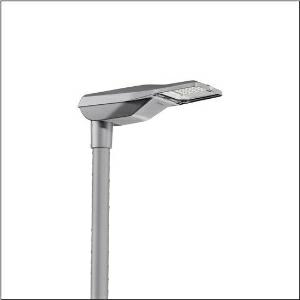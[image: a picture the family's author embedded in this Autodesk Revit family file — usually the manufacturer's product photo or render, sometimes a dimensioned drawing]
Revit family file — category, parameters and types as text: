
# Revit family: streetlight_sl_21_iq_micro___p0_5a_5xe1v31g08cb_6456
name_source: partatom
category: Lighting Fixtures
units: mm (PartAtom-declared; Revit-internal decimal feet)

## family parameters
Cut with Voids When Loaded = No
Host = Face
Light Source = No
Part Type = Normal
Room Calculation Point = No
Round Connector Dimension = Use Diameter
Shared = No

## types (1)
- --- (1 x LED, 2780 lm, 19.4 W, 3000K)
    Apparent Load = 19 VA
    CIE Flux Codes = 37 73 96 100 100
    Color Rendering = 70
    Color Temperature = 3000K
    Default Elevation = 1800 mm
    Description = Streetlight SL 21 iQ micro, mast luminaire, primary light control with lens, of PMMA, primary optical cover: cover, of toughened safety glass, transparent, light distribution: P0.5a, light emission: direct distribution, primary light characteristic: asymmetric, installation type: post-top, side-entry, LED, High Power LED, rated luminous flux: 2.780lm, luminous efficacy: 143lm/W, light colour: 730, colour temperature: 3000K, control gear: iQ Street-Remote, control: pre-setting: linear dimming characteristic, Street-Remote, Auto-Match, Temp-Guard, Lumen-Switch, Night-Set, Smart-Wire, Light-Fading, Desk-Remote (wireless, voltage-free reading and setting of iQ features in the workshop via application-optimized NFC function/RFID function), optimised constant luminous flux control (CLO 2.0), mains connection: 220..240V, AC, 50/60Hz, start of lifetime: 19W, end of service life: 20W, reduction: 10W, luminaire housing, of diecast aluminium, powder-coated, Siteco® metallic grey (DB 702S), corrosivity category C5 mid according to DIN EN ISO 12944, please order mast flange separately, inclination adjustable: 0°, 5°, 10°, 15°, sealing non-destructively replaceable, multi-level sealing system, length: 528mm, width: 235mm, height: 110mm, mast flange for spigot size: 42mm (side-entry): 5XC10008XM4, 60/48mm (side-entry/post-top): 5XC10108XM2, 76/60mm (side-entry/post-top): 5XC10108XM1, protection rating (complete): IP66, insulation class (complete): insulation class II (safety insulation), certification: CE, ENEC, ENEC+, VDE, impact resistance: IK10, permissible operating ambient temperature for outdoor applications: -40..+50°C, standard-compliant lighting for roads and squares, packaging unit: 1 piece

Light Distribution: P0.5a
    Height = 110 mm
    Lamp = 1 x LED
    Lamp Light Flux = 2780 lm
    Lamp Power = 19.4 W
    Lamp count = 1
    Length = 528 mm
    Luminous efficacy = 143 lm/W
    Manufacturer = Siteco
    ModVariant = No
    Model = 5XE1V31G08CB
    Number of Poles = 1
    OnlyDefault = Yes
    Power Factor = 1
    Product Name = Streetlight SL 21 iQ micro | P0.5a
    Product group = mast luminaire | pylon top
    ProductGroupID = 6100
    Protection Class = Protection class II
    Protection Degree = IP 66
    RLX_Detail_Level = 1
    RLX_Emergency_Light_Flux = 0 lm
    RLX_Emergency_Type = 0
    RLX_Emergency_Type_DB = No
    RlxData = <blob elided: 98949 chars, md5=77d16221>
    Socket = socket
    Standby Power = 0 W
    System Light Flux = 2780 lm
    System Power = 19 W
    Type Comments = factory setting: luminous flux: 100 % | dim-lin: 254 | 387 mA
    Type Image = l_1006881.jpg
    URL = http://relux.com
    VarID = @adj_091817
    Voltage = 0 V
    Weight = 0.00 kg
    Width = 235 mm

## geometry (parser evidence)
native form markers: Blend x4, Sweep x10
no freeform markers — native parametric forms only
